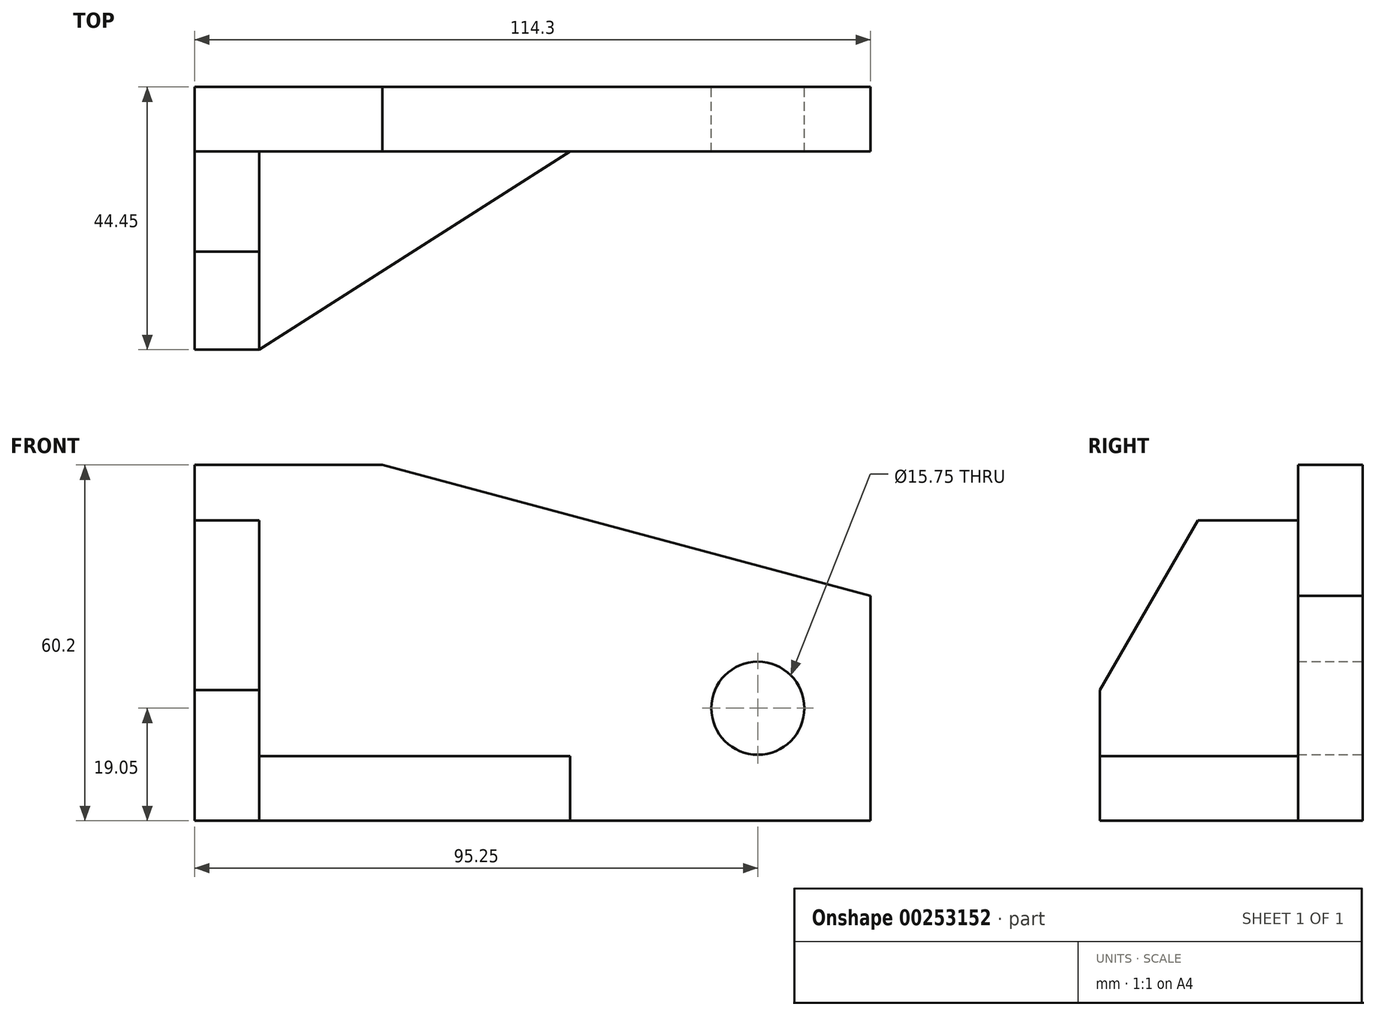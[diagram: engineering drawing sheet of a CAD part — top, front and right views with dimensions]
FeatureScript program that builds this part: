
annotation { "Feature Type Name" : "Feature", "Feature Type Description" : "" }
export const myFeature = defineFeature(function(context is Context, id is Id, definition is map)
    precondition{}
    {
        {
            var Q0;
            Q0=qCreatedBy(makeId("Front.planeOp"),FACE);
            var sketch = newSketch(context, id + "F0", { "sketchPlane" : qUnion([Q0])});
            skLineSegment(sketch, "E0", {"start": v(0, 60.2) * mm, "end": v(31.75, 60.2) * mm});
            skLineSegment(sketch, "E1", {"start": v(31.75, 60.2) * mm, "end": v(114.3, 38.08) * mm});
            skLineSegment(sketch, "E2", {"start": v(114.3, 38.08) * mm, "end": v(114.3, 0) * mm});
            skLineSegment(sketch, "E3", {"start": v(114.3, 0) * mm, "end": v(0, 0) * mm});
            skLineSegment(sketch, "E4", {"start": v(0, 0) * mm, "end": v(0, 60.2) * mm});
            skLineSegment(sketch, "E5", {"start": v(31.75, 60.2) * mm, "end": v(114.3, 60.2) * mm, "construction": true});
            skCircle(sketch, "E6", {"center": v(95.25, 19.05) * mm, "radius": 7.87 * mm});
            skLineSegment(sketch, "E7", {"start": v(95.25, 19.05) * mm, "end": v(95.25, 0) * mm, "construction": true});
            skSolve(sketch);
        }
        {
            var Q0;
            Q0=makeQuery(id+"F0.imprint","IMPRINT",FACE,{"disambiguationData":[TD([[makeQuery(id+"F0.imprint","IMPRINT",EDGE,{"derivedFrom":sQuery(id+"F0.wireOp",EDGE,"E0")}),-1.0]])]});
            extrude(context, id + "F1", {"entities" : qUnion([Q0]), "depth" : 10.92 * mm});
        }
        {
            var Q0;
            Q0=qCreatedBy(makeId("Right.planeOp"),FACE);
            var sketch = newSketch(context, id + "F2", { "sketchPlane" : qUnion([Q0])});
            skLineSegment(sketch, "E8", {"start": v(-44.45, 0) * mm, "end": v(-44.45, 22.1) * mm});
            skLineSegment(sketch, "E9", {"start": v(-44.45, 0) * mm, "end": v(-10.92, 0) * mm});
            skLineSegment(sketch, "E10", {"start": v(-10.92, 50.8) * mm, "end": v(-27.88, 50.8) * mm});
            skLineSegment(sketch, "E11", {"start": v(-27.88, 50.8) * mm, "end": v(-44.45, 22.1) * mm});
            skLineSegment(sketch, "E12", {"start": v(-44.45, 22.1) * mm, "end": v(-44.45, 50.8) * mm, "construction": true});
            skLineSegment(sketch, "E13", {"start": v(-10.92, 50.8) * mm, "end": v(-10.92, 0) * mm});
            skSolve(sketch);
        }
        {
            var Q0;
            Q0=qCreatedBy(makeId("Top.planeOp"),FACE);
            var sketch = newSketch(context, id + "F3", { "sketchPlane" : qUnion([Q0])});
            skLineSegment(sketch, "E14", {"start": v(10.92, -10.92) * mm, "end": v(63.5, -10.92) * mm});
            skLineSegment(sketch, "E15", {"start": v(63.5, -10.92) * mm, "end": v(10.92, -44.45) * mm});
            skLineSegment(sketch, "E16", {"start": v(10.92, -44.45) * mm, "end": v(10.92, -10.92) * mm});
            skSolve(sketch);
        }
        {
            var Q0;
            Q0=makeQuery(id+"F3.imprint","IMPRINT",FACE,{"disambiguationData":[TD([[makeQuery(id+"F3.imprint","IMPRINT",EDGE,{"derivedFrom":sQuery(id+"F3.wireOp",EDGE,"E14")}),-1.0]])]});
            extrude(context, id + "F4", {"entities" : qUnion([Q0]), "operationType" : NewBodyOperationType.ADD, "depth" : 10.92 * mm});
        }
        {
            var Q0;
            Q0=makeQuery(id+"F2.imprint","IMPRINT",FACE,{"disambiguationData":[TD([[makeQuery(id+"F2.imprint","IMPRINT",EDGE,{"derivedFrom":sQuery(id+"F2.wireOp",EDGE,"E8")}),-1.0]])]});
            extrude(context, id + "F5", {"entities" : qUnion([Q0]), "operationType" : NewBodyOperationType.ADD, "depth" : 10.92 * mm});
        }
    });
